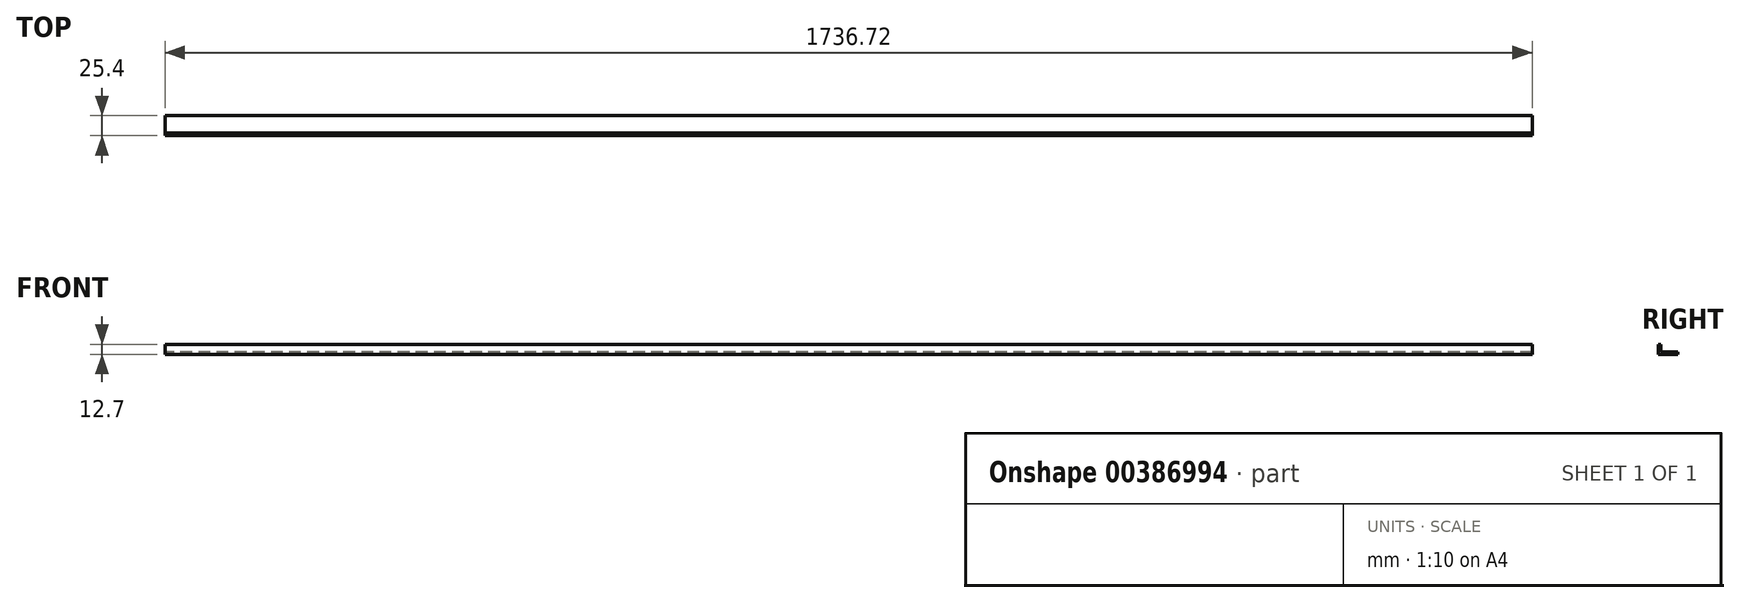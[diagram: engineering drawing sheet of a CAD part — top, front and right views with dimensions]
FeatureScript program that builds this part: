
annotation { "Feature Type Name" : "Feature", "Feature Type Description" : "" }
export const myFeature = defineFeature(function(context is Context, id is Id, definition is map)
    precondition{}
    {
        {
            var Q0;
            Q0=qCreatedBy(makeId("Right.planeOp"),FACE);
            var sketch = newSketch(context, id + "F0", { "sketchPlane" : qUnion([Q0])});
            skLineSegment(sketch, "E0", {"start": v(0, 0) * mm, "end": v(-22.23, 0) * mm});
            skLineSegment(sketch, "E1", {"start": v(-22.23, 0) * mm, "end": v(-22.23, 9.52) * mm});
            skLineSegment(sketch, "E2.0", {"start": v(-25.4, -3.18) * mm, "end": v(-25.4, 9.52) * mm});
            skLineSegment(sketch, "E2.1", {"start": v(0, -3.17) * mm, "end": v(-25.4, -3.18) * mm});
            skLineSegment(sketch, "E3", {"start": v(-22.23, 9.52) * mm, "end": v(-25.4, 9.52) * mm});
            skLineSegment(sketch, "E4", {"start": v(0, -3.17) * mm, "end": v(0, 0) * mm});
            skSolve(sketch);
        }
        {
            var Q0;
            Q0 = qSketchRegion(id + "F0", true);
            extrude(context, id + "F1", {"entities" : qUnion([Q0]), "endBound" : BoundingType.SYMMETRIC, "depth" : 1736.72 * mm, "offsetDistance" : 25.4 * mm});
        }
    });
